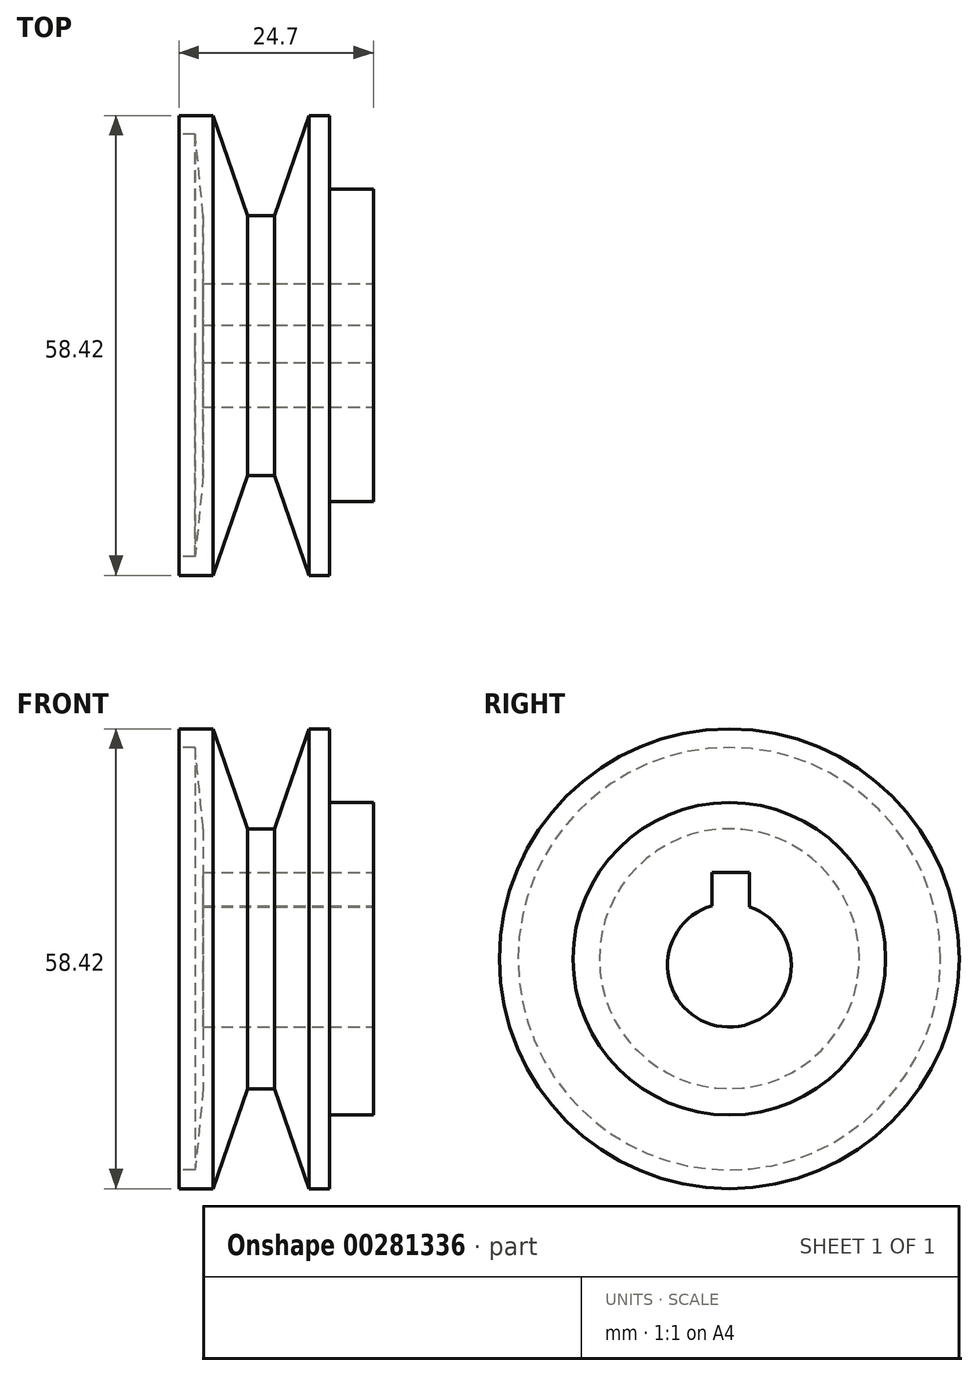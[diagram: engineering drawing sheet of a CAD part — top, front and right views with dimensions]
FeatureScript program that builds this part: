
annotation { "Feature Type Name" : "Feature", "Feature Type Description" : "" }
export const myFeature = defineFeature(function(context is Context, id is Id, definition is map)
    precondition{}
    {
        {
            var Q0;
            Q0=qCreatedBy(makeId("Front.planeOp"),FACE);
            var sketch = newSketch(context, id + "F0", { "sketchPlane" : qUnion([Q0])});
            skLineSegment(sketch, "E0", {"start": v(0, 0) * mm, "end": v(-2.45, 0) * mm});
            skLineSegment(sketch, "E1", {"start": v(-2.45, 0) * mm, "end": v(-6.82, 12.7) * mm});
            skLineSegment(sketch, "E2", {"start": v(-6.82, 12.7) * mm, "end": v(-11.14, 12.7) * mm});
            skLineSegment(sketch, "E3", {"start": v(-11.14, 12.7) * mm, "end": v(-11.14, 10.32) * mm});
            skLineSegment(sketch, "E4", {"start": v(-11.14, 10.32) * mm, "end": v(-9.09, 10.32) * mm});
            skLineSegment(sketch, "E5", {"start": v(-9.09, 10.32) * mm, "end": v(-8.06, 0) * mm});
            skLineSegment(sketch, "E6", {"start": v(8, 0) * mm, "end": v(8, 12.7) * mm});
            skLineSegment(sketch, "E7", {"start": v(8, 12.7) * mm, "end": v(5.37, 12.7) * mm});
            skLineSegment(sketch, "E8", {"start": v(5.37, 12.7) * mm, "end": v(1, 0) * mm});
            skLineSegment(sketch, "E9", {"start": v(1, 0) * mm, "end": v(0, 0) * mm});
            skLineSegment(sketch, "E10", {"start": v(-2.45, 0) * mm, "end": v(1, 0) * mm});
            skLineSegment(sketch, "E11", {"start": v(-8.06, 0) * mm, "end": v(-8.06, -16.51) * mm});
            skLineSegment(sketch, "E12", {"start": v(-8.06, -16.51) * mm, "end": v(8, -16.51) * mm});
            skLineSegment(sketch, "E13", {"start": v(8, -16.51) * mm, "end": v(8, 0) * mm});
            skSolve(sketch);
        }
        {
            var Q0;
            Q0=makeQuery(id+"F0.imprint","IMPRINT",FACE,{"disambiguationData":[TD([[makeQuery(id+"F0.imprint","IMPRINT",EDGE,{"derivedFrom":sQuery(id+"F0.wireOp",EDGE,"E1")}),1.0]])]});
            var Q1;
            Q1=sQuery(id+"F0.wireOp",EDGE,"E12");
            revolve(context, id + "F1", {"entities" : qUnion([Q0]), "axis" : qUnion([Q1]), "revolveType" : RevolveType.FULL});
        }
        {
            var Q0;
            Q0=makeQuery(id+"F1.opRevolve","SWEPT_FACE",FACE,{"disambiguationData":[OSD([sQuery(id+"F0.wireOp",EDGE,"E6"),sQuery(id+"F0.wireOp",EDGE,"E13")])]});
            var sketch = newSketch(context, id + "F2", { "sketchPlane" : qUnion([Q0])});
            skPoint(sketch, "E14.startSnap0", {"position": v(0, -16.51) * mm});
            skCircle(sketch, "E15", {"center": v(0, -16.51) * mm, "radius": 19.85 * mm});
            skSolve(sketch);
        }
        {
            var Q0;
            Q0 = qSketchRegion(id + "F2", true);
            extrude(context, id + "F3", {"entities" : qUnion([Q0]), "operationType" : NewBodyOperationType.ADD, "depth" : 5.56 * mm});
        }
        {
            var Q0;
            Q0=makeQuery(id+"F3.opExtrude","CAP_FACE",FACE,{"disambiguationData":[OSD([sQuery(id+"F2.wireOp",EDGE,"E15")])],"isStart":false});
            var sketch = newSketch(context, id + "F4", { "sketchPlane" : qUnion([Q0])});
            skPoint(sketch, "E16.startSnap0", {"position": v(0, -17.33) * mm});
            skArc(sketch, "E17", {"start": v(-2.2, -9.78) * mm, "mid": v(-0.2, -25.19) * mm, "end": v(2.6, -9.9) * mm});
            skLineSegment(sketch, "E18", {"start": v(-2.2, -9.78) * mm, "end": v(-2.2, -5.58) * mm});
            skLineSegment(sketch, "E19", {"start": v(-2.2, -5.58) * mm, "end": v(2.6, -5.58) * mm});
            skLineSegment(sketch, "E20", {"start": v(2.6, -5.58) * mm, "end": v(2.6, -9.9) * mm});
            skSolve(sketch);
        }
        {
            var Q0;
            Q0=makeQuery(id+"F4.imprint","IMPRINT",FACE,{"disambiguationData":[TD([[makeQuery(id+"F4.imprint","IMPRINT",EDGE,{"derivedFrom":sQuery(id+"F4.wireOp",EDGE,"E17")}),1.0]])]});
            extrude(context, id + "F5", {"entities" : qUnion([Q0]), "operationType" : NewBodyOperationType.REMOVE, "oppositeDirection" : true, "depth" : 254 * mm});
        }
    });
